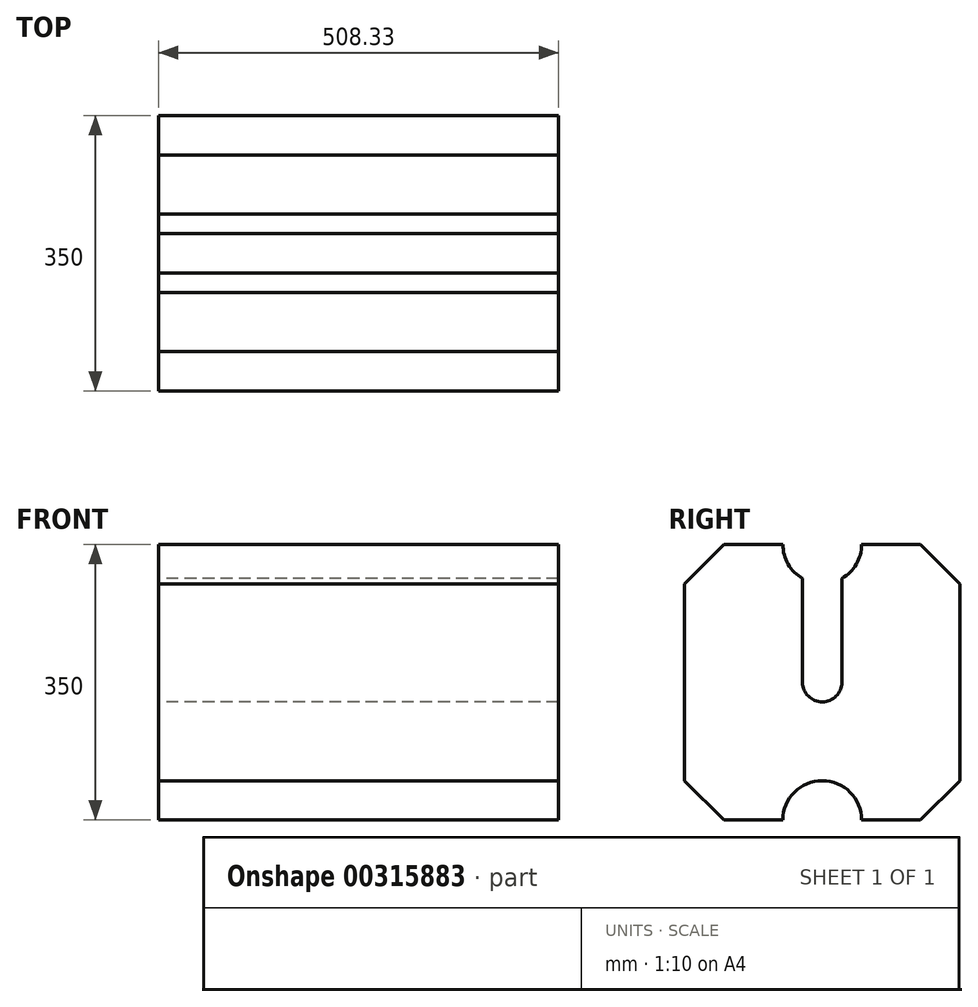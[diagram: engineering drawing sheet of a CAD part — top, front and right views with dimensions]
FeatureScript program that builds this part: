
annotation { "Feature Type Name" : "Feature", "Feature Type Description" : "" }
export const myFeature = defineFeature(function(context is Context, id is Id, definition is map)
    precondition{}
    {
        {
            var Q0;
            Q0=qCreatedBy(makeId("Right.planeOp"),FACE);
            var sketch = newSketch(context, id + "F0", { "sketchPlane" : qUnion([Q0])});
            skLineSegment(sketch, "E0.bottom", {"start": v(125, 175) * mm, "end": v(50, 175) * mm});
            skLineSegment(sketch, "E0.top", {"start": v(125, -175) * mm, "end": v(50, -175) * mm});
            skLineSegment(sketch, "E0.left", {"start": v(175, 125) * mm, "end": v(175, -125) * mm});
            skLineSegment(sketch, "E0.right", {"start": v(-175, 125) * mm, "end": v(-175, -125) * mm});
            skPoint(sketch, "E0.middle", {"position": v(0, 0) * mm});
            skLineSegment(sketch, "E1", {"start": v(-175, 125) * mm, "end": v(-125, 175) * mm});
            skLineSegment(sketch, "E2", {"start": v(-175, -125) * mm, "end": v(-125, -175) * mm});
            skLineSegment(sketch, "E3", {"start": v(125, -175) * mm, "end": v(175, -125) * mm});
            skLineSegment(sketch, "E4", {"start": v(175, 125) * mm, "end": v(125, 175) * mm});
            skPoint(sketch, "E5.orphan", {"position": v(-175, 175) * mm});
            skPoint(sketch, "E6.orphan", {"position": v(175, 175) * mm});
            skPoint(sketch, "E7.orphan", {"position": v(175, -175) * mm});
            skPoint(sketch, "E8.orphan", {"position": v(-175, -175) * mm});
            skLineSegment(sketch, "E9", {"start": v(-175, -125) * mm, "end": v(175, -125) * mm, "construction": true});
            skLineSegment(sketch, "E10", {"start": v(-175, 125) * mm, "end": v(175, 125) * mm, "construction": true});
            skLineSegment(sketch, "E11", {"start": v(-125, 175) * mm, "end": v(-125, -175) * mm, "construction": true});
            skLineSegment(sketch, "E12", {"start": v(125, 175) * mm, "end": v(125, -175) * mm, "construction": true});
            skArc(sketch, "E13", {"start": v(-50, 175) * mm, "mid": v(0, 125) * mm, "end": v(50, 175) * mm});
            skArc(sketch, "E14", {"start": v(50, -175) * mm, "mid": v(0, -125) * mm, "end": v(-50, -175) * mm});
            skLineSegment(sketch, "E15", {"start": v(0, 125) * mm, "end": v(0, -25) * mm});
            skLineSegment(sketch, "E16.0", {"start": v(-25, 131.7) * mm, "end": v(-25, -131.7) * mm});
            skLineSegment(sketch, "E17.0", {"start": v(25, 131.7) * mm, "end": v(25, -131.7) * mm});
            skArc(sketch, "E18", {"start": v(-25, 0) * mm, "mid": v(0, -25) * mm, "end": v(25, 0) * mm});
            skLineSegment(sketch, "E19.trimOffspring", {"start": v(-50, 175) * mm, "end": v(-125, 175) * mm});
            skLineSegment(sketch, "E20.trimOffspring", {"start": v(-50, -175) * mm, "end": v(-125, -175) * mm});
            skSolve(sketch);
        }
        {
            var Q0;
            Q0=qCreatedBy(makeId("Front.planeOp"),FACE);
            var sketch = newSketch(context, id + "F1", { "sketchPlane" : qUnion([Q0])});
            skLineSegment(sketch, "E21", {"start": v(0, 0) * mm, "end": v(-147.8, 0) * mm});
            skLineSegment(sketch, "E22", {"start": v(-147.8, 0) * mm, "end": v(-211.39, 15.25) * mm});
            skLineSegment(sketch, "E23", {"start": v(-211.39, 15.25) * mm, "end": v(-297.46, 16.6) * mm});
            skLineSegment(sketch, "E24", {"start": v(-297.46, 16.6) * mm, "end": v(-506.6, 10.57) * mm});
            skLineSegment(sketch, "E25", {"start": v(0, 0) * mm, "end": v(-508.33, 0) * mm});
            skSolve(sketch);
        }
        {
            var Q0;
            {var subQ4=sQuery(id+"F0.wireOp",EDGE,"E0.bottom");Q0=makeQuery(id+"F0.imprint","IMPRINT",FACE,{"disambiguationData":[TD([[makeQuery(id+"F0.imprint","IMPRINT",EDGE,{"derivedFrom":subQ4}),1.0]])]});}
            var Q1;
            {var subQ2=sQuery(id+"F0.wireOp",EDGE,"E16.0");var subQ5=sQuery(id+"F0.wireOp",EDGE,"E14");var subQ8=makeQuery(id+"F0.imprint","INTERSECT",VERTEX,{"derivedFrom":[subQ5,subQ2]});Q1=makeQuery(id+"F0.imprint","IMPRINT",FACE,{"disambiguationData":[TD([[makeQuery(id+"F0.imprint","IMPRINT",EDGE,{"disambiguationData":[TD([[subQ8,1.0]])],"derivedFrom":subQ5}),-1.0]])]});}
            var Q2;
            Q2=makeQuery(id+"F0.imprint","IMPRINT",FACE,{"disambiguationData":[TD([[makeQuery(id+"F0.imprint","IMPRINT",EDGE,{"derivedFrom":sQuery(id+"F0.wireOp",EDGE,"E0.right")}),1.0]])]});
            var Q3;
            Q3=sQuery(id+"F1.wireOp",EDGE,"E25");
            sweep(context, id + "F2", {"profiles" : qUnion([Q0, Q1, Q2]), "path" : qUnion([Q3])});
        }
    });
